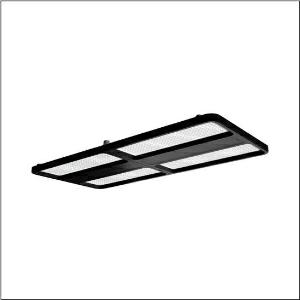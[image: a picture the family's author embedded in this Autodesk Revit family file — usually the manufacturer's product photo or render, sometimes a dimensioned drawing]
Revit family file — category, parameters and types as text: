
# Revit family: highbay_21_maxi_52hn31db4tda
name_source: partatom
category: Lighting Fixtures
units: mm (PartAtom-declared; Revit-internal decimal feet)

## family parameters
Cut with Voids When Loaded = No
Host = Face
Light Source = No
Part Type = Normal
Room Calculation Point = No
Round Connector Dimension = Use Diameter
Shared = No

## types (1)
- --- (1 x LED, 8350 lm, 44.8 W, 4000K)
    Apparent Load = 45 VA
    CIE Flux Codes = 89 97 99 100 100
    Color Rendering = 80
    Color Temperature = 4000K
    Default Elevation = 1800 mm
    Description = high bay luminaire Highbay 21 maxi; direct symmetric narrow distribution, light control with lens of PMMA; UGR ≤ 22 (X = 4H | Y = 8H | S = 0.25H | reflection values 70/50/20); luminous flux: 53.000lm; light colour: 840, colour temperature: 4000K, MacAdam ≤ 3 SDCM (initial), colour rendering: CRI > 80; luminous efficacy: 184,9lm/W; rated service life: 75.000h (L80) at AT= ta max; control: DALI 2; luminaire connection: terminal, 5-pole, max. 2.5mm² (cable entry for one cable, Ø 8.5..16mm); mains connection: 230..240V, AC/DC 0/50..60Hz; connected load: 286,6W; protection rating (complete): IP66; insulation class (complete): insulation class I (protective earthing); protection symbol: D; impact resistance: IK08; certification: CE, ENEC, VDE, UKCA; luminaire for central battery installations according to EN 60598-2-22, internal wiring halogen-free; luminaire LABS conformity tested according to VDMA 24364:2018-05; Suitable for use in the food industry according to the specifications of IFS-Food, HACCP and/or BRC; housing frame of high-performance plastic PA6, matt jet black (RAL 9005); cover of PMMA; dimension (LxWxH): 946 x 442 x 72mm; permissible operating ambient temperature: -40..+55°C (reducing of maximum allowable ambient temperature of 5°C with ceiling mounting); packaging unit: 1 piece; (delivery without accessories; please order mounting accessories separately)
    Height = 72 mm  [stored 0.23622 ft]
    Lamp = 1 x LED
    Lamp Light Flux = 8350 lm
    Lamp Power = 44.8 W
    Lamp count = 1
    Length = 946 mm
    Luminous efficacy = 186 lm/W
    Manufacturer = Siteco
    ModVariant = No
    Model = 52HN31DB4TDA
    Mounting Place = Ceiling
    Mounting Type = Pendant
    Number of Poles = 1
    OnlyDefault = Yes
    Power Factor = 1
    Product Name = Highbay 21 maxi
    Product group = high bay luminaire
    ProductGroupID = 902
    Protection Class = Protection class I
    Protection Degree = IP 66
    RLX_Detail_Level = 1
    RLX_Emergency_Light_Flux = 0 lm
    RLX_Emergency_Type = 0
    RLX_Emergency_Type_DB = No
    RlxData = <blob elided: 133429 chars, md5=747e10a6>
    Socket = socket
    Standby Power = 0 W
    System Light Flux = 8350 lm
    System Power = 45 W
    Type Comments = : DC mode (central or group accumulator) initial emergency light level
    Type Image = l_1378821.jpg
    URL = http://relux.com
    VarID = @adj_017759
    Voltage = 0 V
    Weight = 0.00 kg
    Width = 442 mm

note: [stored X ft] marks values corroborated as IEEE doubles in the binary element streams (Revit-internal decimal feet)

## geometry (parser evidence)
native form markers: Blend x4, Sweep x9
no freeform markers — native parametric forms only
